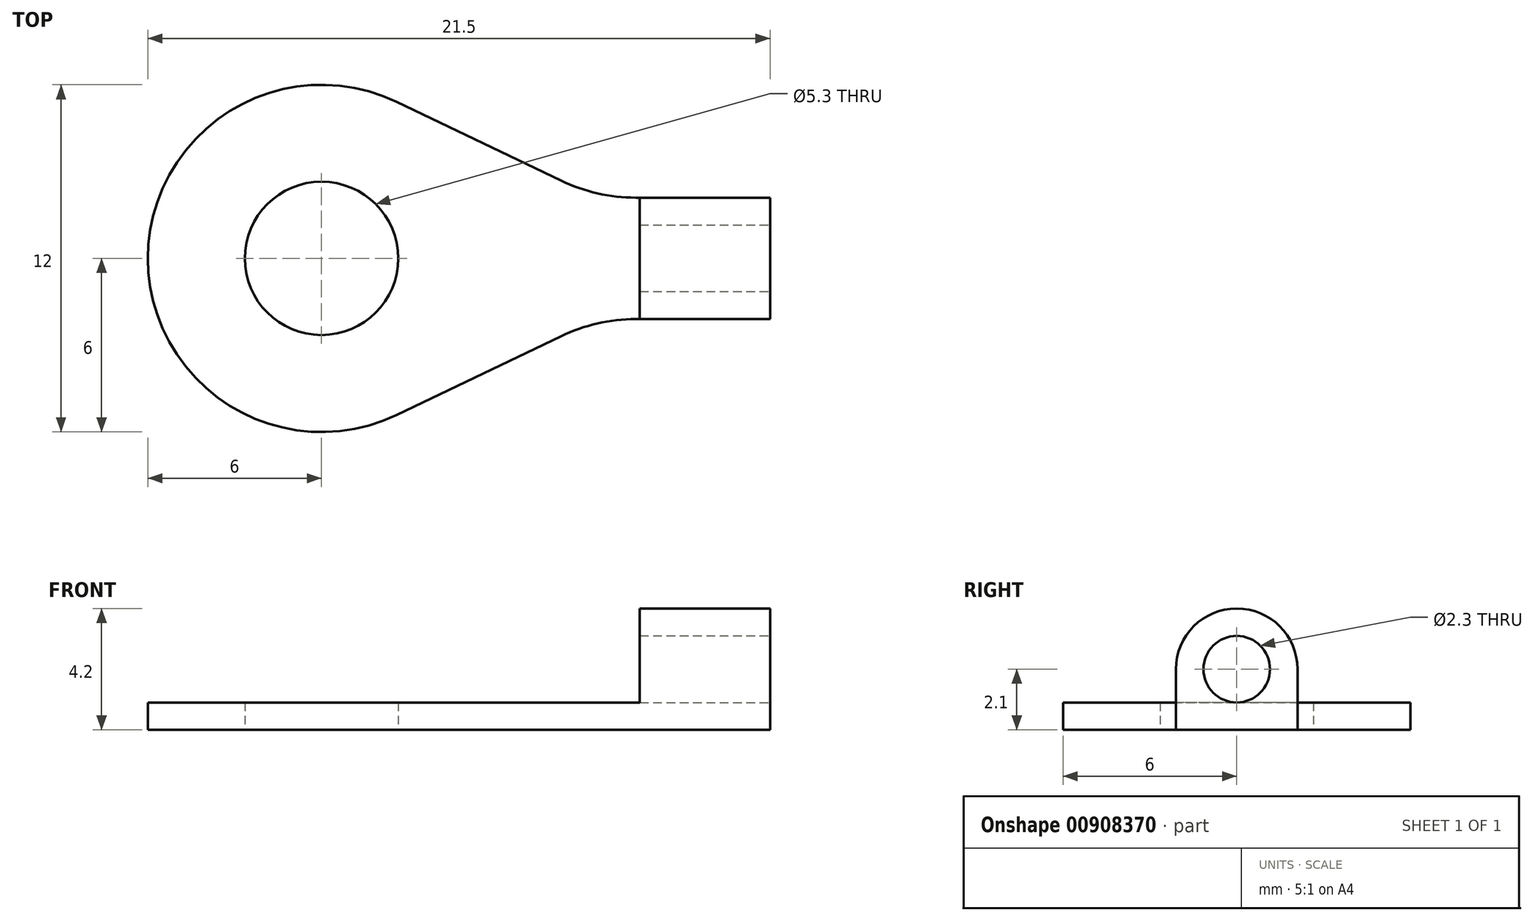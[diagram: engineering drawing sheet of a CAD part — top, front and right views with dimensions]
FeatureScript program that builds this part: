
annotation { "Feature Type Name" : "Feature", "Feature Type Description" : "" }
export const myFeature = defineFeature(function(context is Context, id is Id, definition is map)
    precondition{}
    {
        {
            var Q0;
            Q0=qCreatedBy(makeId("Top.planeOp"),FACE);
            var sketch = newSketch(context, id + "F0", { "sketchPlane" : qUnion([Q0])});
            skLineSegment(sketch, "E0.left", {"start": v(0, 6) * mm, "end": v(0, 6) * mm});
            skLineSegment(sketch, "E0.right", {"start": v(21.5, 3.9) * mm, "end": v(21.5, 8.1) * mm});
            skPoint(sketch, "E1.visualSharp", {"position": v(0, 12) * mm});
            skArc(sketch, "E1.filletArc", {"start": v(6, 12) * mm, "mid": v(1.76, 10.24) * mm, "end": v(0, 6) * mm});
            skPoint(sketch, "E2.visualSharp", {"position": v(0, 0) * mm});
            skArc(sketch, "E2.filletArc", {"start": v(0, 6) * mm, "mid": v(1.76, 1.76) * mm, "end": v(6, 0) * mm});
            skLineSegment(sketch, "E3.bottom", {"start": v(21.5, 3.9) * mm, "end": v(16.86, 3.9) * mm});
            skLineSegment(sketch, "E3.top", {"start": v(21.5, 8.1) * mm, "end": v(16.86, 8.1) * mm});
            skPoint(sketch, "E3.middle", {"position": v(21.5, 6) * mm});
            skArc(sketch, "E4", {"start": v(8.6, 11.41) * mm, "mid": v(0, 6) * mm, "end": v(8.6, 0.59) * mm});
            skCircle(sketch, "E5", {"center": v(6, 6) * mm, "radius": 2.65 * mm});
            skLineSegment(sketch, "E6", {"start": v(14.27, 8.69) * mm, "end": v(8.6, 11.41) * mm});
            skLineSegment(sketch, "E7", {"start": v(14.27, 3.31) * mm, "end": v(8.6, 0.59) * mm});
            skPoint(sketch, "E8.visualSharp", {"position": v(15.5, 8.1) * mm});
            skArc(sketch, "E8.filletArc", {"start": v(14.27, 8.69) * mm, "mid": v(15.53, 8.25) * mm, "end": v(16.86, 8.1) * mm});
            skPoint(sketch, "E9.visualSharp", {"position": v(15.5, 3.9) * mm});
            skArc(sketch, "E9.filletArc", {"start": v(16.86, 3.9) * mm, "mid": v(15.53, 3.75) * mm, "end": v(14.27, 3.31) * mm});
            skPoint(sketch, "E10.orphan", {"position": v(26, 8.1) * mm});
            skPoint(sketch, "E11.orphan", {"position": v(26, 3.9) * mm});
            skPoint(sketch, "E0.top.end.orphan", {"position": v(21.5, 12) * mm});
            skPoint(sketch, "E0.bottom.end.orphan", {"position": v(21.5, 0) * mm});
            skPoint(sketch, "E3.right.end.orphan", {"position": v(17, 8.1) * mm});
            skPoint(sketch, "E3.right.start.orphan", {"position": v(17, 3.9) * mm});
            skSolve(sketch);
        }
        {
            var Q0;
            Q0=makeQuery(id+"F0.imprint","IMPRINT",FACE,{"disambiguationData":[TD([[makeQuery(id+"F0.imprint","IMPRINT",EDGE,{"derivedFrom":sQuery(id+"F0.wireOp",EDGE,"E0.right")}),1.0]])]});
            extrude(context, id + "F1", {"entities" : qUnion([Q0]), "depth" : 0.95 * mm, "offsetDistance" : 25 * mm});
        }
        {
            var Q0;
            Q0=makeQuery(id+"F1.opExtrude","CAP_FACE",FACE,{"disambiguationData":[OSD([sQuery(id+"F0.wireOp",EDGE,"E0.right"),sQuery(id+"F0.wireOp",EDGE,"E3.bottom"),sQuery(id+"F0.wireOp",EDGE,"E3.top"),sQuery(id+"F0.wireOp",EDGE,"E4"),sQuery(id+"F0.wireOp",EDGE,"E5"),sQuery(id+"F0.wireOp",EDGE,"E6"),sQuery(id+"F0.wireOp",EDGE,"E7"),sQuery(id+"F0.wireOp",EDGE,"E8.filletArc"),sQuery(id+"F0.wireOp",EDGE,"E9.filletArc")])],"isStart":false});
            var sketch = newSketch(context, id + "F2", { "sketchPlane" : qUnion([Q0])});
            skLineSegment(sketch, "E12.bottom", {"start": v(21.5, 8.1) * mm, "end": v(17, 8.1) * mm});
            skLineSegment(sketch, "E12.top", {"start": v(21.5, 3.9) * mm, "end": v(17, 3.9) * mm});
            skLineSegment(sketch, "E12.left", {"start": v(21.5, 8.1) * mm, "end": v(21.5, 3.9) * mm});
            skLineSegment(sketch, "E12.right", {"start": v(17, 8.1) * mm, "end": v(17, 3.9) * mm});
            skSolve(sketch);
        }
        {
            var Q0;
            Q0=makeQuery(id+"F2.imprint","IMPRINT",FACE,{"disambiguationData":[TD([[makeQuery(id+"F2.imprint","IMPRINT",EDGE,{"derivedFrom":sQuery(id+"F2.wireOp",EDGE,"E12.bottom")}),1.0]])]});
            extrude(context, id + "F3", {"entities" : qUnion([Q0]), "operationType" : NewBodyOperationType.ADD, "depth" : 3.25 * mm, "offsetDistance" : 25 * mm});
        }
        {
            var Q0;
            Q0=makeQuery(id+"F3.opExtrude","CAP_EDGE",EDGE,{"disambiguationData":[OSD([sQuery(id+"F2.wireOp",EDGE,"E12.bottom")])],"isStart":false});
            var Q1;
            Q1=makeQuery(id+"F3.opExtrude","CAP_EDGE",EDGE,{"disambiguationData":[OSD([sQuery(id+"F2.wireOp",EDGE,"E12.top")])],"isStart":false});
            fillet(context, id + "F4", {"entities" : qUnion([Q0, Q1]), "radius" : 2.1 * mm, "tangentPropagation" : true, "allowEdgeOverflow" : false});
        }
        {
            var Q0;
            Q0=makeQuery(id+"F3.boolean.opBoolean","MERGE",FACE,{"derivedFrom":[makeQuery(id+"F1.opExtrude","SWEPT_FACE",FACE,{"disambiguationData":[OSD([sQuery(id+"F0.wireOp",EDGE,"E0.right")])]}),makeQuery(id+"F3.opExtrude","SWEPT_FACE",FACE,{"disambiguationData":[OSD([sQuery(id+"F2.wireOp",EDGE,"E12.left")])]})]});
            var sketch = newSketch(context, id + "F5", { "sketchPlane" : qUnion([Q0])});
            skCircle(sketch, "E13", {"center": v(6, 2.1) * mm, "radius": 1.15 * mm});
            skSolve(sketch);
        }
        {
            var Q0;
            Q0=makeQuery(id+"F5.imprint","IMPRINT",FACE,{"disambiguationData":[TD([[makeQuery(id+"F5.imprint","IMPRINT",EDGE,{"derivedFrom":sQuery(id+"F5.wireOp",EDGE,"E13")}),1.0]])]});
            extrude(context, id + "F6", {"entities" : qUnion([Q0]), "operationType" : NewBodyOperationType.REMOVE, "oppositeDirection" : true, "depth" : 25 * mm, "offsetDistance" : 25 * mm});
        }
    });
